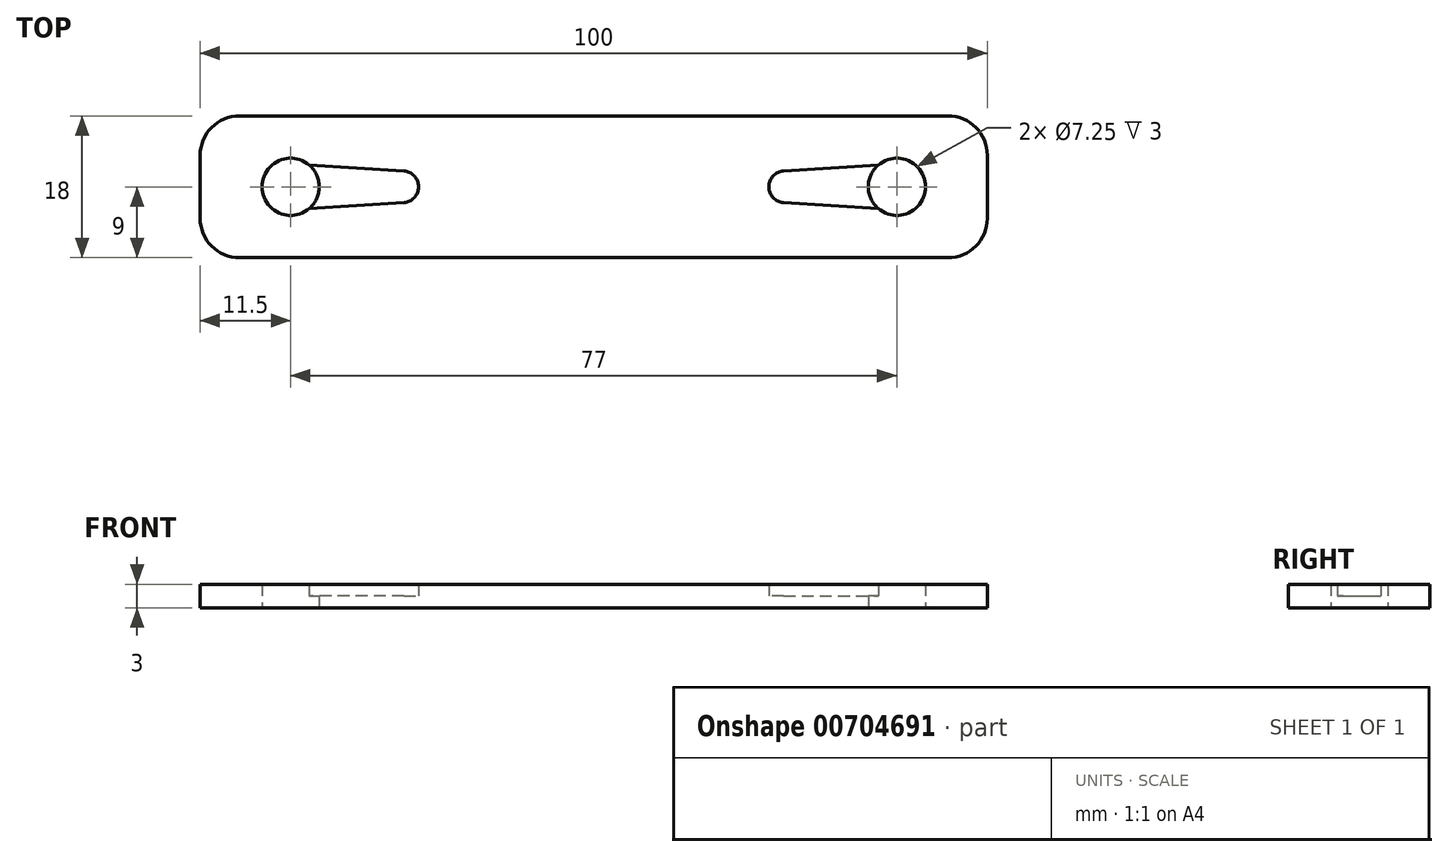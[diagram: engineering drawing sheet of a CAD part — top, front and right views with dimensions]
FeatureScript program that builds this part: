
annotation { "Feature Type Name" : "Feature", "Feature Type Description" : "" }
export const myFeature = defineFeature(function(context is Context, id is Id, definition is map)
    precondition{}
    {
        {
            var Q0;
            Q0=qCreatedBy(makeId("Top.planeOp"),FACE);
            var sketch = newSketch(context, id + "F0", { "sketchPlane" : qUnion([Q0])});
            skLineSegment(sketch, "E0.bottom", {"start": v(-50, 9) * mm, "end": v(50, 9) * mm});
            skLineSegment(sketch, "E0.top", {"start": v(-50, -9) * mm, "end": v(50, -9) * mm});
            skLineSegment(sketch, "E0.left", {"start": v(-50, 9) * mm, "end": v(-50, -9) * mm});
            skLineSegment(sketch, "E0.right", {"start": v(50, 9) * mm, "end": v(50, -9) * mm});
            skCircle(sketch, "E1", {"center": v(-38.5, 0) * mm, "radius": 3.62 * mm});
            skCircle(sketch, "E2", {"center": v(-24.25, 0) * mm, "radius": 2 * mm});
            skLineSegment(sketch, "E3", {"start": v(-24.12, 2) * mm, "end": v(-36.14, 2.75) * mm});
            skLineSegment(sketch, "E4", {"start": v(-24.12, -2) * mm, "end": v(-36.14, -2.75) * mm});
            skCircle(sketch, "E5", {"center": v(38.5, 0) * mm, "radius": 3.62 * mm});
            skCircle(sketch, "E6", {"center": v(24.25, 0) * mm, "radius": 2 * mm});
            skLineSegment(sketch, "E7", {"start": v(24.12, -2) * mm, "end": v(36.14, -2.75) * mm});
            skLineSegment(sketch, "E8", {"start": v(24.12, 2) * mm, "end": v(36.14, 2.75) * mm});
            skLineSegment(sketch, "E9", {"start": v(-42.13, 5.12) * mm, "end": v(-42.13, -5) * mm, "construction": true});
            skLineSegment(sketch, "E10", {"start": v(-22.25, 4.43) * mm, "end": v(-22.25, -5.04) * mm, "construction": true});
            skSolve(sketch);
        }
        {
            var Q0;
            Q0=makeQuery(id+"F0.imprint","IMPRINT",FACE,{"disambiguationData":[TD([[makeQuery(id+"F0.imprint","IMPRINT",EDGE,{"derivedFrom":sQuery(id+"F0.wireOp",EDGE,"E0.bottom")}),-1.0]])]});
            extrude(context, id + "F1", {"entities" : qUnion([Q0]), "depth" : 3 * mm, "offsetDistance" : 25 * mm});
        }
        {
            var Q0;
            Q0=makeQuery(id+"F1.opExtrude","SWEPT_EDGE",EDGE,{"disambiguationData":[OSD([sQuery(id+"F0.wireOp",EDGE,"E0.bottom"),sQuery(id+"F0.wireOp",EDGE,"E0.left")])]});
            var Q1;
            Q1=makeQuery(id+"F1.opExtrude","SWEPT_EDGE",EDGE,{"disambiguationData":[OSD([sQuery(id+"F0.wireOp",EDGE,"E0.top"),sQuery(id+"F0.wireOp",EDGE,"E0.left")])]});
            var Q2;
            Q2=makeQuery(id+"F1.opExtrude","SWEPT_EDGE",EDGE,{"disambiguationData":[OSD([sQuery(id+"F0.wireOp",EDGE,"E0.bottom"),sQuery(id+"F0.wireOp",EDGE,"E0.right")])]});
            var Q3;
            Q3=makeQuery(id+"F1.opExtrude","SWEPT_EDGE",EDGE,{"disambiguationData":[OSD([sQuery(id+"F0.wireOp",EDGE,"E0.top"),sQuery(id+"F0.wireOp",EDGE,"E0.right")])]});
            fillet(context, id + "F2", {"entities" : qUnion([Q0, Q1, Q2, Q3]), "radius" : 5 * mm, "tangentPropagation" : true, "allowEdgeOverflow" : false});
        }
        {
            var Q0;
            {var subQ0=sQuery(id+"F0.wireOp",EDGE,"E3");Q0=makeQuery(id+"F0.imprint","IMPRINT",FACE,{"disambiguationData":[TD([[makeQuery(id+"F0.imprint","IMPRINT",EDGE,{"derivedFrom":subQ0}),1.0]])]});}
            var Q1;
            {var subQ0=sQuery(id+"F0.wireOp",EDGE,"E2");var subQ1=makeQuery(id+"F0.imprint","INTERSECT",VERTEX,{"derivedFrom":[subQ0,sQuery(id+"F0.wireOp",EDGE,"E3")]});Q1=makeQuery(id+"F0.imprint","IMPRINT",FACE,{"disambiguationData":[TD([[makeQuery(id+"F0.imprint","IMPRINT",EDGE,{"disambiguationData":[TD([[subQ1,-1.0]])],"derivedFrom":subQ0}),1.0]])]});}
            extrude(context, id + "F3", {"entities" : qUnion([Q0, Q1]), "operationType" : NewBodyOperationType.ADD, "depth" : 1.5 * mm, "offsetDistance" : 25 * mm});
        }
        {
            var Q0;
            {var subQ0=sQuery(id+"F0.wireOp",EDGE,"E7");Q0=makeQuery(id+"F0.imprint","IMPRINT",FACE,{"disambiguationData":[TD([[makeQuery(id+"F0.imprint","IMPRINT",EDGE,{"derivedFrom":subQ0}),1.0]])]});}
            var Q1;
            {var subQ0=sQuery(id+"F0.wireOp",EDGE,"E6");var subQ1=makeQuery(id+"F0.imprint","INTERSECT",VERTEX,{"derivedFrom":[subQ0,sQuery(id+"F0.wireOp",EDGE,"E7")]});Q1=makeQuery(id+"F0.imprint","IMPRINT",FACE,{"disambiguationData":[TD([[makeQuery(id+"F0.imprint","IMPRINT",EDGE,{"disambiguationData":[TD([[subQ1,-1.0]])],"derivedFrom":subQ0}),1.0]])]});}
            extrude(context, id + "F4", {"entities" : qUnion([Q0, Q1]), "operationType" : NewBodyOperationType.ADD, "depth" : 1.5 * mm, "offsetDistance" : 25 * mm});
        }
    });
